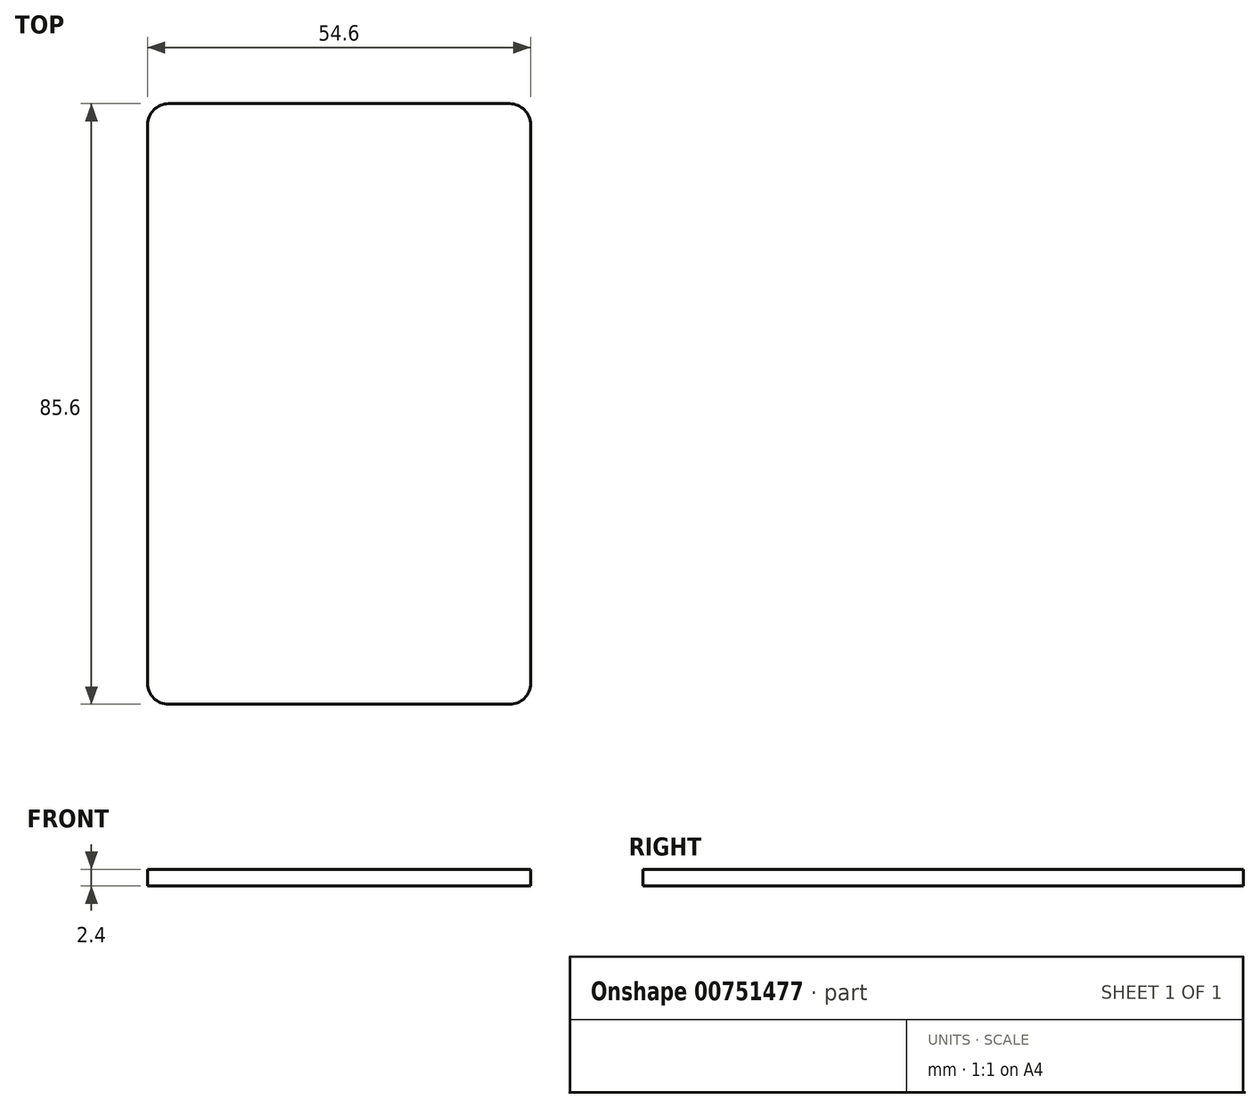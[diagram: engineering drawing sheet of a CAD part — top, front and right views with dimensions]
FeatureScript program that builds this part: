
annotation { "Feature Type Name" : "Feature", "Feature Type Description" : "" }
export const myFeature = defineFeature(function(context is Context, id is Id, definition is map)
    precondition{}
    {
        {
            var Q0;
            Q0=qCreatedBy(makeId("Top.planeOp"),FACE);
            var sketch = newSketch(context, id + "F0", { "sketchPlane" : qUnion([Q0])});
            skLineSegment(sketch, "E0.bottom", {"start": v(3, 85.6) * mm, "end": v(51.6, 85.6) * mm});
            skLineSegment(sketch, "E0.top", {"start": v(3, 0) * mm, "end": v(51.6, 0) * mm});
            skLineSegment(sketch, "E0.left", {"start": v(0, 82.6) * mm, "end": v(0, 3) * mm});
            skLineSegment(sketch, "E0.right", {"start": v(54.6, 82.6) * mm, "end": v(54.6, 3) * mm});
            skPoint(sketch, "E1.visualSharp", {"position": v(0, 85.6) * mm});
            skArc(sketch, "E1.filletArc", {"start": v(3, 85.6) * mm, "mid": v(0.88, 84.72) * mm, "end": v(0, 82.6) * mm});
            skPoint(sketch, "E2.visualSharp", {"position": v(54.6, 85.6) * mm});
            skArc(sketch, "E2.filletArc", {"start": v(54.6, 82.6) * mm, "mid": v(53.72, 84.72) * mm, "end": v(51.6, 85.6) * mm});
            skPoint(sketch, "E3.visualSharp", {"position": v(54.6, 0) * mm});
            skArc(sketch, "E3.filletArc", {"start": v(51.6, 0) * mm, "mid": v(53.72, 0.88) * mm, "end": v(54.6, 3) * mm});
            skPoint(sketch, "E4.visualSharp", {"position": v(0, 0) * mm});
            skArc(sketch, "E4.filletArc", {"start": v(0, 3) * mm, "mid": v(0.88, 0.88) * mm, "end": v(3, 0) * mm});
            skSolve(sketch);
        }
        {
            var Q0;
            Q0=qSketchRegion(id+"F0",true);
            extrude(context, id + "F1", {"entities" : qUnion([Q0]), "depth" : 2.4 * mm});
        }
    });
